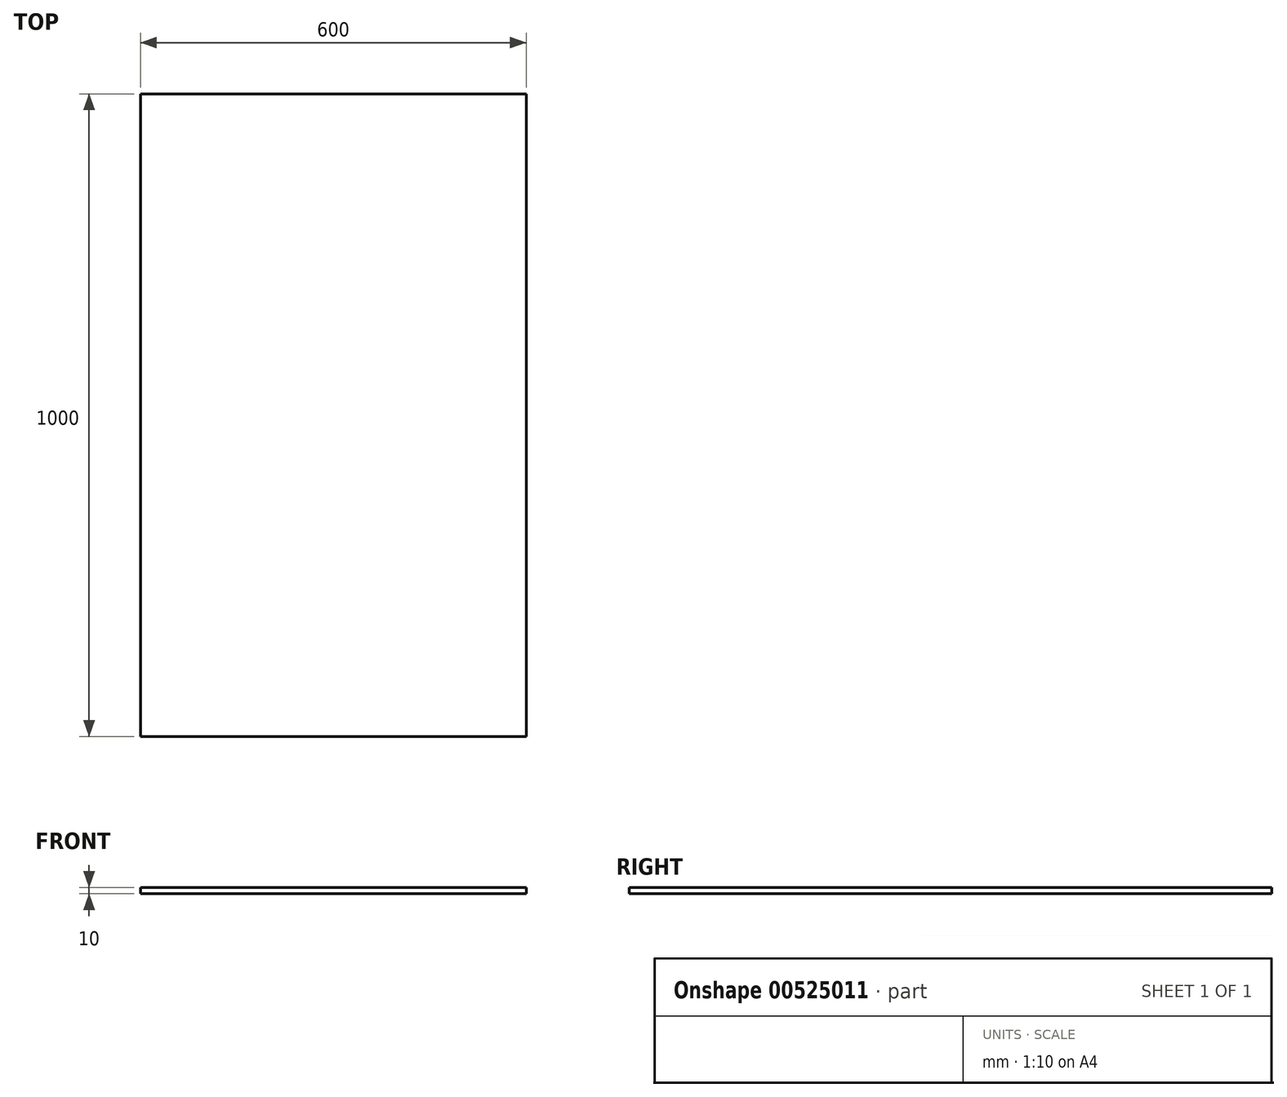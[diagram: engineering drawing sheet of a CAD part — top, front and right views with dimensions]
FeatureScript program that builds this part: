
annotation { "Feature Type Name" : "Feature", "Feature Type Description" : "" }
export const myFeature = defineFeature(function(context is Context, id is Id, definition is map)
    precondition{}
    {
        {
            var Q0;
            Q0=qCreatedBy(makeId("Top.planeOp"),FACE);
            var sketch = newSketch(context, id + "F0", { "sketchPlane" : qUnion([Q0])});
            skLineSegment(sketch, "E0.bottom", {"start": v(300, 500) * mm, "end": v(-300, 500) * mm});
            skLineSegment(sketch, "E0.top", {"start": v(300, -500) * mm, "end": v(-300, -500) * mm});
            skLineSegment(sketch, "E0.left", {"start": v(300, 500) * mm, "end": v(300, -500) * mm});
            skLineSegment(sketch, "E0.right", {"start": v(-300, 500) * mm, "end": v(-300, -500) * mm});
            skPoint(sketch, "E0.middle", {"position": v(0, 0) * mm});
            skSolve(sketch);
        }
        {
            var Q0;
            Q0 = qSketchRegion(id + "F0", true);
            extrude(context, id + "F1", {"entities" : qUnion([Q0]), "endBound" : BoundingType.SYMMETRIC, "depth" : 10 * mm, "offsetDistance" : 25 * mm});
        }
    });
